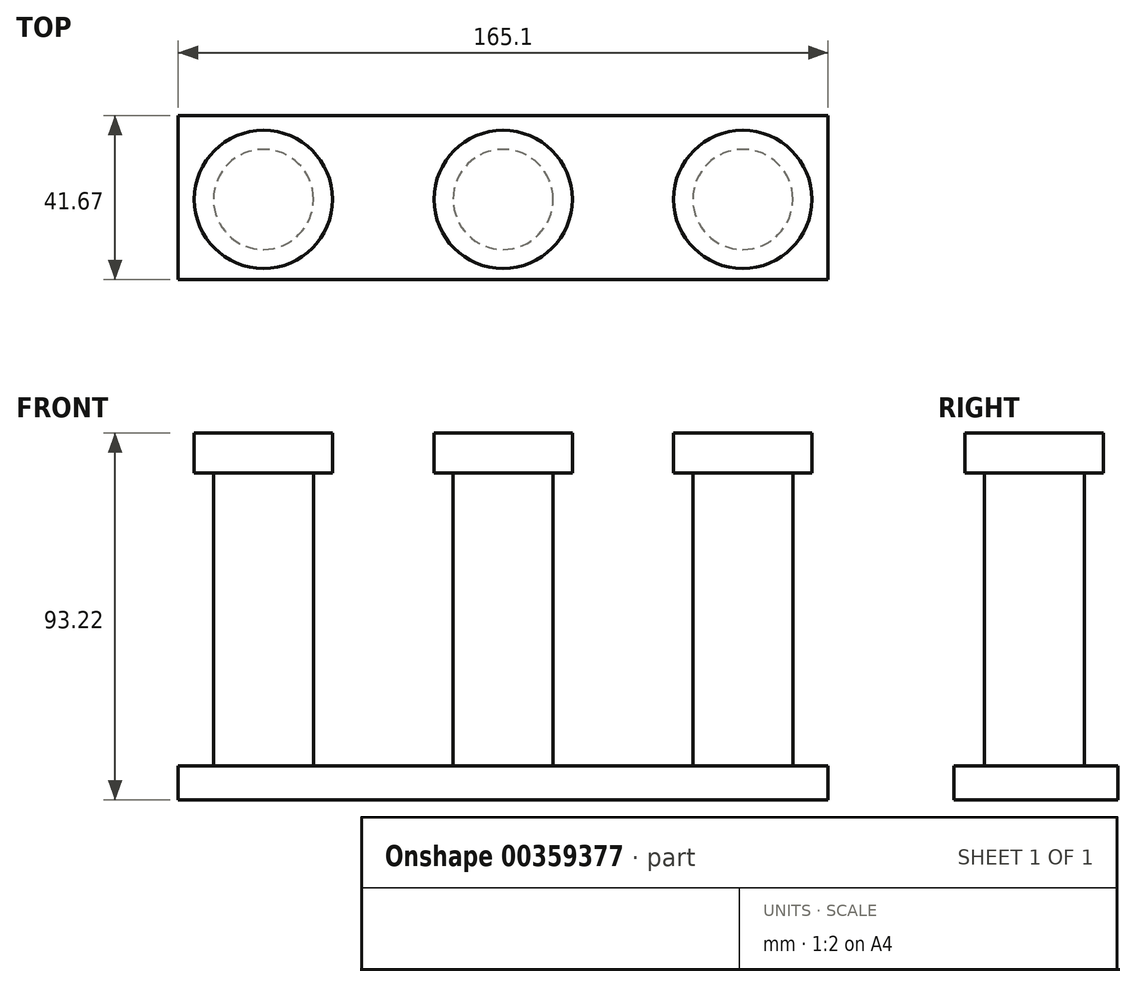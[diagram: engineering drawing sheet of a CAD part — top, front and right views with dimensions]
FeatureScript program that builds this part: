
annotation { "Feature Type Name" : "Feature", "Feature Type Description" : "" }
export const myFeature = defineFeature(function(context is Context, id is Id, definition is map)
    precondition{}
    {
        {
            var Q0;
            Q0=qCreatedBy(makeId("Top.planeOp"),FACE);
            var sketch = newSketch(context, id + "F0", { "sketchPlane" : qUnion([Q0])});
            skCircle(sketch, "E0", {"center": v(0, 0) * mm, "radius": 12.7 * mm});
            skSolve(sketch);
        }
        {
            var Q0;
            Q0 = qSketchRegion(id + "F0", true);
            extrude(context, id + "F1", {"entities" : qUnion([Q0]), "depth" : 76.2 * mm});
        }
        {
            var Q0;
            Q0=qCreatedBy(makeId("Top.planeOp"),FACE);
            cPlane(context, id + "F2", {"entities" : qUnion([Q0]), "cplaneType" : CPlaneType.OFFSET, "offset" : 74.42 * mm, "width" : 152.4 * mm, "height" : 152.4 * mm});
        }
        {
            var Q0;
            Q0=qCreatedBy(id+"F2.planeOp",FACE);
            var sketch = newSketch(context, id + "F3", { "sketchPlane" : qUnion([Q0])});
            skCircle(sketch, "E1", {"center": v(0, 0) * mm, "radius": 17.56 * mm});
            skSolve(sketch);
        }
        {
            var Q0;
            Q0 = qSketchRegion(id + "F3", true);
            extrude(context, id + "F4", {"entities" : qUnion([Q0]), "operationType" : NewBodyOperationType.ADD, "depth" : 10.16 * mm});
        }
        {
            var Q0;
            Q0=qCreatedBy(makeId("Top.planeOp"),FACE);
            var sketch = newSketch(context, id + "F5", { "sketchPlane" : qUnion([Q0])});
            skLineSegment(sketch, "E2.bottom", {"start": v(-21.66, -20.37) * mm, "end": v(143.44, -20.37) * mm});
            skLineSegment(sketch, "E2.top", {"start": v(-21.66, 21.3) * mm, "end": v(143.44, 21.3) * mm});
            skLineSegment(sketch, "E2.left", {"start": v(-21.66, -20.37) * mm, "end": v(-21.66, 21.3) * mm});
            skLineSegment(sketch, "E2.right", {"start": v(143.44, -20.37) * mm, "end": v(143.44, 21.3) * mm});
            skLineSegment(sketch, "E3", {"start": v(60.9, -20.37) * mm, "end": v(60.9, 21.3) * mm});
            skLineSegment(sketch, "E4", {"start": v(60.9, 21.3) * mm, "end": v(60.9, 0) * mm});
            skLineSegment(sketch, "E5", {"start": v(60.9, 0) * mm, "end": v(60.9, -20.37) * mm});
            skLineSegment(sketch, "E6", {"start": v(60.9, 0) * mm, "end": v(0, 0) * mm});
            skLineSegment(sketch, "E7", {"start": v(60.9, 0) * mm, "end": v(121.77, 0) * mm});
            skSolve(sketch);
        }
        {
            var Q0;
            Q0 = qSketchRegion(id + "F5", true);
            extrude(context, id + "F6", {"entities" : qUnion([Q0]), "operationType" : NewBodyOperationType.ADD, "oppositeDirection" : true, "depth" : 8.64 * mm});
        }
        {
            var Q0;
            Q0=makeQuery(id+"F6.opExtrude","CAP_FACE",FACE,{"disambiguationData":[OSD([sQuery(id+"F5.wireOp",EDGE,"E2.bottom"),sQuery(id+"F5.wireOp",EDGE,"E2.top"),sQuery(id+"F5.wireOp",EDGE,"E2.left"),sQuery(id+"F5.wireOp",EDGE,"E2.right")])],"isStart":true});
            var sketch = newSketch(context, id + "F7", { "sketchPlane" : qUnion([Q0])});
            skCircle(sketch, "E8", {"center": v(60.9, 0) * mm, "radius": 12.7 * mm});
            skCircle(sketch, "E9", {"center": v(121.77, 0) * mm, "radius": 12.7 * mm});
            skPoint(sketch, "E10.start.orphan", {"position": v(60.9, 21.3) * mm});
            skPoint(sketch, "E11.trimOffspring.end.orphan", {"position": v(60.9, -20.37) * mm});
            skSolve(sketch);
        }
        {
            var Q0;
            Q0 = qSketchRegion(id + "F7", true);
            extrude(context, id + "F8", {"entities" : qUnion([Q0]), "operationType" : NewBodyOperationType.ADD, "depth" : 76.2 * mm});
        }
        {
            var Q0;
            Q0=qCreatedBy(id+"F2.planeOp",FACE);
            var sketch = newSketch(context, id + "F9", { "sketchPlane" : qUnion([Q0])});
            skCircle(sketch, "E12", {"center": v(60.9, 0) * mm, "radius": 17.56 * mm});
            skCircle(sketch, "E13", {"center": v(121.77, 0) * mm, "radius": 17.56 * mm});
            skSolve(sketch);
        }
        {
            var Q0;
            Q0 = qSketchRegion(id + "F9", true);
            extrude(context, id + "F10", {"entities" : qUnion([Q0]), "operationType" : NewBodyOperationType.ADD, "depth" : 10.16 * mm});
        }
    });
